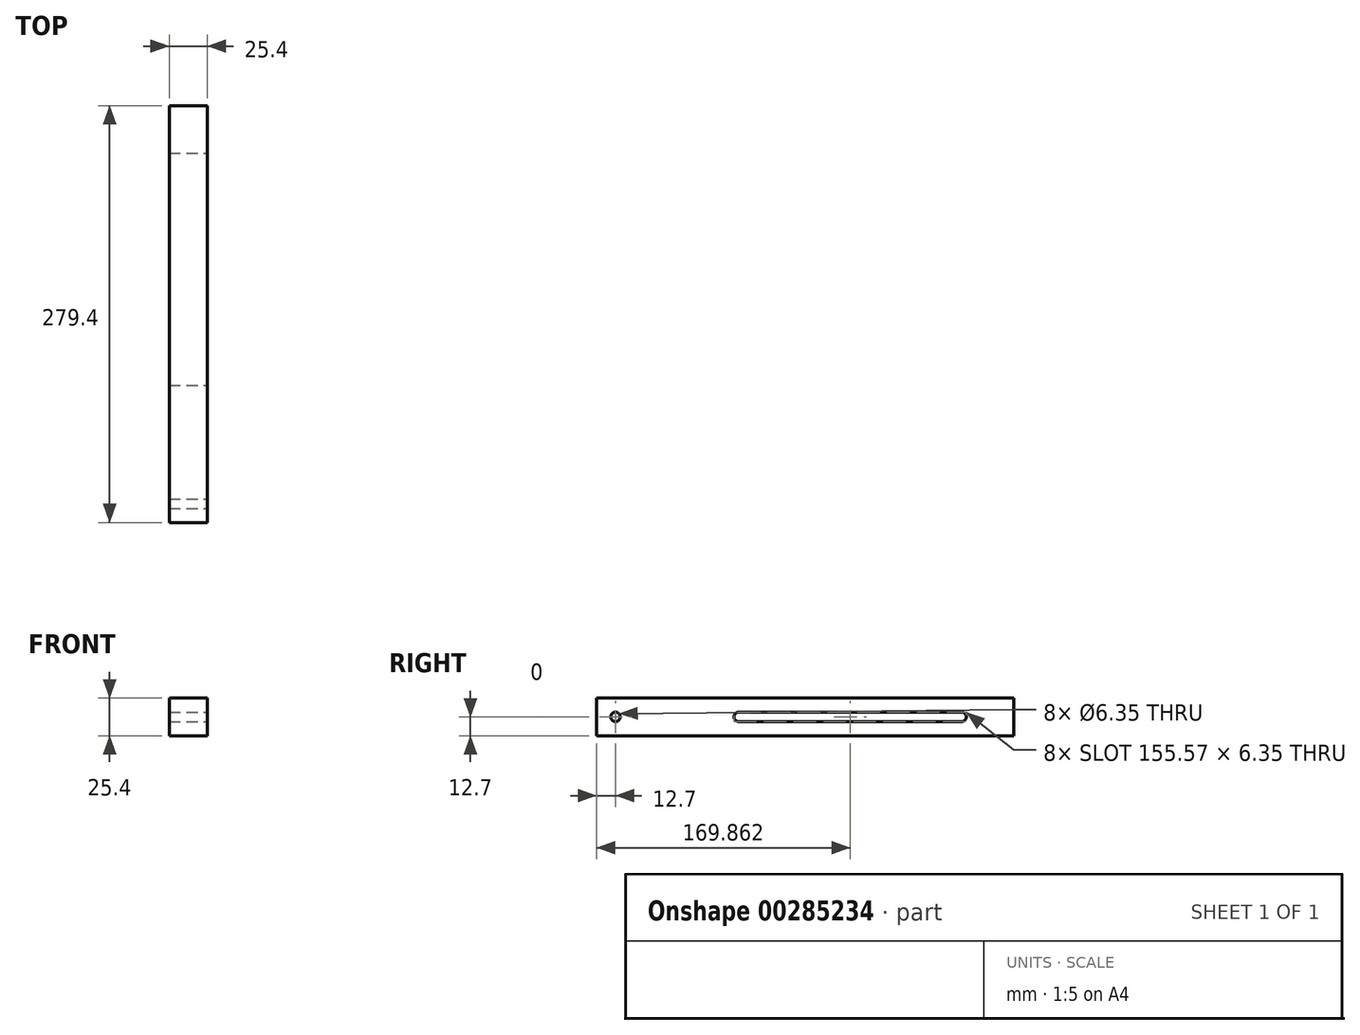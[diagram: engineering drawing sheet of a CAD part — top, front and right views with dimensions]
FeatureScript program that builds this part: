
annotation { "Feature Type Name" : "Feature", "Feature Type Description" : "" }
export const myFeature = defineFeature(function(context is Context, id is Id, definition is map)
    precondition{}
    {
        {
            var Q0;
            Q0=qCreatedBy(makeId("Front.planeOp"),FACE);
            var sketch = newSketch(context, id + "F0", { "sketchPlane" : qUnion([Q0])});
            skLineSegment(sketch, "E0.bottom", {"start": v(0, 0) * mm, "end": v(25.4, 0) * mm});
            skLineSegment(sketch, "E0.top", {"start": v(0, 25.4) * mm, "end": v(25.4, 25.4) * mm});
            skLineSegment(sketch, "E0.left", {"start": v(0, 0) * mm, "end": v(0, 25.4) * mm});
            skLineSegment(sketch, "E0.right", {"start": v(25.4, 0) * mm, "end": v(25.4, 25.4) * mm});
            skSolve(sketch);
        }
        {
            var Q0;
            Q0=makeQuery(id+"F0.imprint","IMPRINT",FACE,{"disambiguationData":[TD([[makeQuery(id+"F0.imprint","IMPRINT",EDGE,{"derivedFrom":sQuery(id+"F0.wireOp",EDGE,"E0.bottom")}),1.0]])]});
            extrude(context, id + "F1", {"entities" : qUnion([Q0]), "depth" : 279.4 * mm});
        }
        {
            var Q0;
            Q0=makeQuery(id+"F1.opExtrude","SWEPT_FACE",FACE,{"disambiguationData":[OSD([sQuery(id+"F0.wireOp",EDGE,"E0.right")])]});
            var sketch = newSketch(context, id + "F2", { "sketchPlane" : qUnion([Q0])});
            skLineSegment(sketch, "E1", {"start": v(-279.4, 12.7) * mm, "end": v(-266.7, 12.7) * mm});
            skLineSegment(sketch, "E2", {"start": v(-266.7, 12.7) * mm, "end": v(-266.7, 0) * mm});
            skCircle(sketch, "E3", {"center": v(-266.7, 12.7) * mm, "radius": 3.18 * mm});
            skLineSegment(sketch, "E4", {"start": v(0, 12.7) * mm, "end": v(-31.75, 12.7) * mm});
            skLineSegment(sketch, "E5", {"start": v(-31.75, 12.7) * mm, "end": v(-31.75, 9.52) * mm});
            skLineSegment(sketch, "E6", {"start": v(-31.75, 9.52) * mm, "end": v(-34.92, 9.52) * mm});
            skLineSegment(sketch, "E7", {"start": v(-34.92, 9.52) * mm, "end": v(-34.92, 15.87) * mm});
            skLineSegment(sketch, "E8", {"start": v(-34.92, 15.87) * mm, "end": v(-31.75, 15.87) * mm});
            skLineSegment(sketch, "E9", {"start": v(-31.75, 15.87) * mm, "end": v(-31.75, 12.7) * mm});
            skLineSegment(sketch, "E10.bottom", {"start": v(-34.92, 9.52) * mm, "end": v(-184.15, 9.52) * mm});
            skLineSegment(sketch, "E10.top", {"start": v(-34.92, 15.87) * mm, "end": v(-184.15, 15.87) * mm});
            skLineSegment(sketch, "E10.right", {"start": v(-184.15, 9.52) * mm, "end": v(-184.15, 15.87) * mm});
            skArc(sketch, "E11", {"start": v(-34.92, 9.52) * mm, "mid": v(-31.75, 12.7) * mm, "end": v(-34.92, 15.87) * mm});
            skArc(sketch, "E12", {"start": v(-184.15, 15.87) * mm, "mid": v(-187.33, 12.7) * mm, "end": v(-184.15, 9.52) * mm});
            skSolve(sketch);
        }
        {
            var Q0;
            {var subQ0=sQuery(id+"F2.wireOp",EDGE,"E2");var subQ1=sQuery(id+"F2.wireOp",EDGE,"E1");var subQ2=makeQuery(id+"F2.imprint","INTERSECT",VERTEX,{"derivedFrom":[subQ1,subQ0]});Q0=makeQuery(id+"F2.imprint","IMPRINT",FACE,{"disambiguationData":[TD([[makeQuery(id+"F2.imprint","IMPRINT",EDGE,{"disambiguationData":[TD([[subQ2,1.0]])],"derivedFrom":subQ1}),1.0]])]});}
            var Q1;
            {var subQ0=sQuery(id+"F2.wireOp",EDGE,"E2");var subQ1=sQuery(id+"F2.wireOp",EDGE,"E1");var subQ2=makeQuery(id+"F2.imprint","INTERSECT",VERTEX,{"derivedFrom":[subQ1,subQ0]});Q1=makeQuery(id+"F2.imprint","IMPRINT",FACE,{"disambiguationData":[TD([[makeQuery(id+"F2.imprint","IMPRINT",EDGE,{"disambiguationData":[TD([[subQ2,1.0]])],"derivedFrom":subQ1}),-1.0]])]});}
            var Q2;
            Q2=makeQuery(id+"F2.imprint","IMPRINT",FACE,{"disambiguationData":[TD([[makeQuery(id+"F2.imprint","IMPRINT",EDGE,{"derivedFrom":sQuery(id+"F2.wireOp",EDGE,"E10.right")}),1.0]])]});
            var Q3;
            Q3=makeQuery(id+"F2.imprint","IMPRINT",FACE,{"disambiguationData":[TD([[makeQuery(id+"F2.imprint","IMPRINT",EDGE,{"derivedFrom":sQuery(id+"F2.wireOp",EDGE,"E10.bottom")}),-1.0]])]});
            var Q4;
            {var subQ0=sQuery(id+"F2.wireOp",EDGE,"E7");Q4=makeQuery(id+"F2.imprint","IMPRINT",FACE,{"disambiguationData":[TD([[makeQuery(id+"F2.imprint","IMPRINT",EDGE,{"derivedFrom":subQ0}),-1.0]])]});}
            extrude(context, id + "F3", {"entities" : qUnion([Q0, Q1, Q2, Q3, Q4]), "operationType" : NewBodyOperationType.REMOVE, "oppositeDirection" : true, "depth" : 25.4 * mm});
        }
    });
